# Revit family: Puerta Deslizante 2 hojas
name_source: partatom
category: Doors
revit_build: Autodesk Revit 2017 (Build: 20190508_0315(x64)
units: mm (PartAtom-declared; Revit-internal decimal feet)

## family parameters
Always vertical = Yes
Cut with Voids When Loaded = No
Host = Wall
OmniClass Number = 23.30.10.00
OmniClass Title = Doors
Room Calculation Point = No
Shared = No

## types (1)
- Puerta Deslizante 2 hojas
    Analytic Construction = <None>
    Ancho Riel = 6040 mm  [stored 19.8163 ft]
    Control Alto Puerta = 3000 mm  [stored 9.84252 ft]
    Control Ancho Puerta = 3000 mm  [stored 9.84252 ft]
    Description = Deslizante 2 Hojas
    Espesor = 202 mm
    Frame Projection Ext. = 25 mm  [stored 0.082021 ft]
    Frame Projection Int. = 25 mm  [stored 0.082021 ft]
    Frame Width = 75 mm  [stored 0.246063 ft]
    Function = Interior
    Height = 3050 mm  [stored 10.0066 ft]
    Manufacturer = G-U
    Model = Deslizante 2 Hojas
    Perfil Riel = Stainless Steel AISI 304
    Riel = Stainless Steel AISI 304
    Tipo = Deslizante
    Tope de Puerta = Stainless Steel AISI 304
    URL = http://www.automatics.cl
    Vidrio = Glass
    Wall Closure = By host
    Width = 3020 mm  [stored 9.90814 ft]

note: [stored X ft] marks values corroborated as IEEE doubles in the binary element streams (Revit-internal decimal feet)

## geometry (parser evidence)
native form markers: Sweep x8
no freeform markers — native parametric forms only
